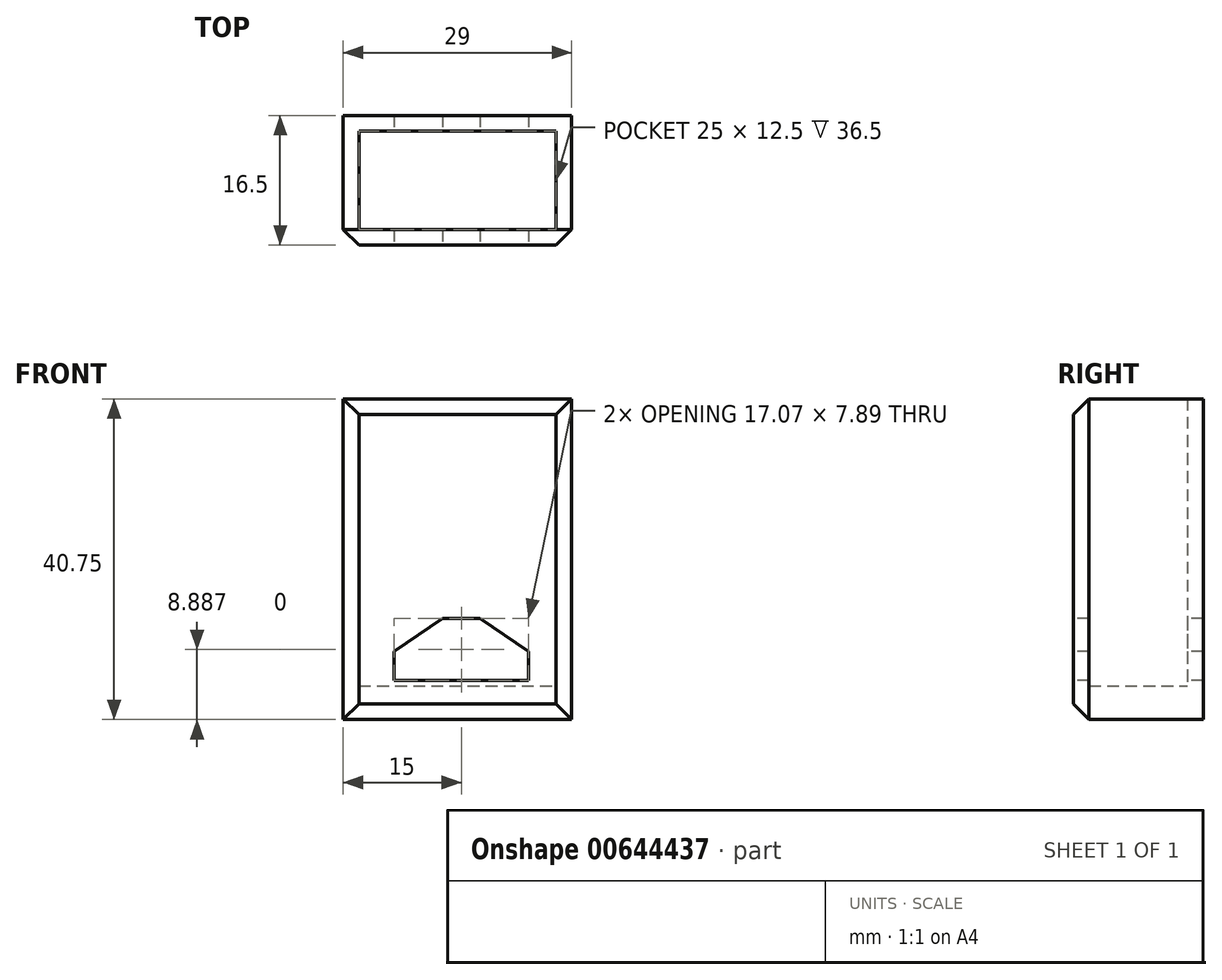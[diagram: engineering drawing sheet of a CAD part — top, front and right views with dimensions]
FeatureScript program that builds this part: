
annotation { "Feature Type Name" : "Feature", "Feature Type Description" : "" }
export const myFeature = defineFeature(function(context is Context, id is Id, definition is map)
    precondition{}
    {
        {
            var Q0;
            Q0=qCreatedBy(makeId("Top.planeOp"),FACE);
            var sketch = newSketch(context, id + "F0", { "sketchPlane" : qUnion([Q0])});
            skLineSegment(sketch, "E0.bottom", {"start": v(0, 0) * mm, "end": v(29, 0) * mm});
            skLineSegment(sketch, "E0.top", {"start": v(0, 16.5) * mm, "end": v(29, 16.5) * mm});
            skLineSegment(sketch, "E0.left", {"start": v(0, 0) * mm, "end": v(0, 16.5) * mm});
            skLineSegment(sketch, "E0.right", {"start": v(29, 0) * mm, "end": v(29, 16.5) * mm});
            skSolve(sketch);
        }
        {
            var Q0;
            Q0 = qSketchRegion(id + "F0", true);
            extrude(context, id + "F1", {"entities" : qUnion([Q0]), "depth" : 38.5 * mm, "offsetDistance" : 25 * mm});
        }
        {
            var Q0;
            Q0=makeQuery(id+"F1.opExtrude","CAP_FACE",FACE,{"disambiguationData":[OSD([sQuery(id+"F0.wireOp",EDGE,"E0.bottom"),sQuery(id+"F0.wireOp",EDGE,"E0.top"),sQuery(id+"F0.wireOp",EDGE,"E0.left"),sQuery(id+"F0.wireOp",EDGE,"E0.right")])],"isStart":false});
            shell(context, id + "F2", {"entities" : qUnion([Q0]), "thickness" : 2 * mm});
        }
        {
            var Q0;
            Q0=makeQuery(id+"F1.opExtrude","CAP_FACE",FACE,{"disambiguationData":[OSD([sQuery(id+"F0.wireOp",EDGE,"E0.bottom"),sQuery(id+"F0.wireOp",EDGE,"E0.top"),sQuery(id+"F0.wireOp",EDGE,"E0.left"),sQuery(id+"F0.wireOp",EDGE,"E0.right")])],"isStart":true});
            extrude(context, id + "F3", {"entities" : qUnion([Q0]), "operationType" : NewBodyOperationType.ADD, "depth" : 2.25 * mm, "offsetDistance" : 25 * mm});
        }
        {
            var Q0;
            {var subQ0=sQuery(id+"F0.wireOp",EDGE,"E0.right");var subQ1=sQuery(id+"F0.wireOp",EDGE,"E0.bottom");Q0=makeQuery(id+"F3.boolean.opBoolean","MERGE",EDGE,{"derivedFrom":[makeQuery(id+"F1.opExtrude","SWEPT_EDGE",EDGE,{"disambiguationData":[OSD([subQ1,subQ0])]}),makeQuery(id+"F3.opExtrude","SWEPT_EDGE",EDGE,{"disambiguationData":[OSD([subQ1,subQ0])]})]});}
            var Q1;
            {var subQ0=sQuery(id+"F0.wireOp",EDGE,"E0.left");var subQ1=sQuery(id+"F0.wireOp",EDGE,"E0.bottom");Q1=makeQuery(id+"F3.boolean.opBoolean","MERGE",EDGE,{"derivedFrom":[makeQuery(id+"F1.opExtrude","SWEPT_EDGE",EDGE,{"disambiguationData":[OSD([subQ1,subQ0])]}),makeQuery(id+"F3.opExtrude","SWEPT_EDGE",EDGE,{"disambiguationData":[OSD([subQ1,subQ0])]})]});}
            var Q2;
            Q2=makeQuery(id+"F1.opExtrude","CAP_EDGE",EDGE,{"disambiguationData":[OSD([sQuery(id+"F0.wireOp",EDGE,"E0.bottom")])],"isStart":false});
            var Q3;
            Q3=makeQuery(id+"F3.opExtrude","CAP_EDGE",EDGE,{"disambiguationData":[OSD([sQuery(id+"F0.wireOp",EDGE,"E0.bottom")])],"isStart":false});
            chamfer(context, id + "F4", {"entities" : qUnion([Q0, Q1, Q2, Q3]), "width" : 2 * mm, "tangentPropagation" : true});
        }
        {
            var Q0;
            {var subQ0=sQuery(id+"F0.wireOp",EDGE,"E0.bottom");Q0=makeQuery(id+"F3.boolean.opBoolean","MERGE",FACE,{"derivedFrom":[makeQuery(id+"F1.opExtrude","SWEPT_FACE",FACE,{"disambiguationData":[OSD([subQ0])]}),makeQuery(id+"F3.opExtrude","SWEPT_FACE",FACE,{"disambiguationData":[OSD([subQ0])]})]});}
            var sketch = newSketch(context, id + "F5", { "sketchPlane" : qUnion([Q0])});
            skLineSegment(sketch, "E1", {"start": v(12.63, 10.58) * mm, "end": v(17.36, 10.58) * mm});
            skLineSegment(sketch, "E2", {"start": v(12.64, 10.58) * mm, "end": v(6.46, 6.41) * mm});
            skLineSegment(sketch, "E3", {"start": v(6.46, 6.41) * mm, "end": v(6.46, 2.7) * mm});
            skLineSegment(sketch, "E4", {"start": v(6.46, 2.7) * mm, "end": v(23.54, 2.7) * mm});
            skLineSegment(sketch, "E5", {"start": v(23.54, 2.7) * mm, "end": v(23.54, 6.41) * mm});
            skLineSegment(sketch, "E6", {"start": v(23.54, 6.41) * mm, "end": v(17.36, 10.58) * mm});
            skSolve(sketch);
        }
        {
            var Q0;
            Q0=makeQuery(id+"F5.imprint","IMPRINT",FACE,{"disambiguationData":[TD([[makeQuery(id+"F5.imprint","IMPRINT",EDGE,{"derivedFrom":sQuery(id+"F5.wireOp",EDGE,"E1")}),-1.0]])]});
            extrude(context, id + "F6", {"entities" : qUnion([Q0]), "operationType" : NewBodyOperationType.REMOVE, "oppositeDirection" : true, "depth" : 25 * mm, "offsetDistance" : 25 * mm});
        }
    });
